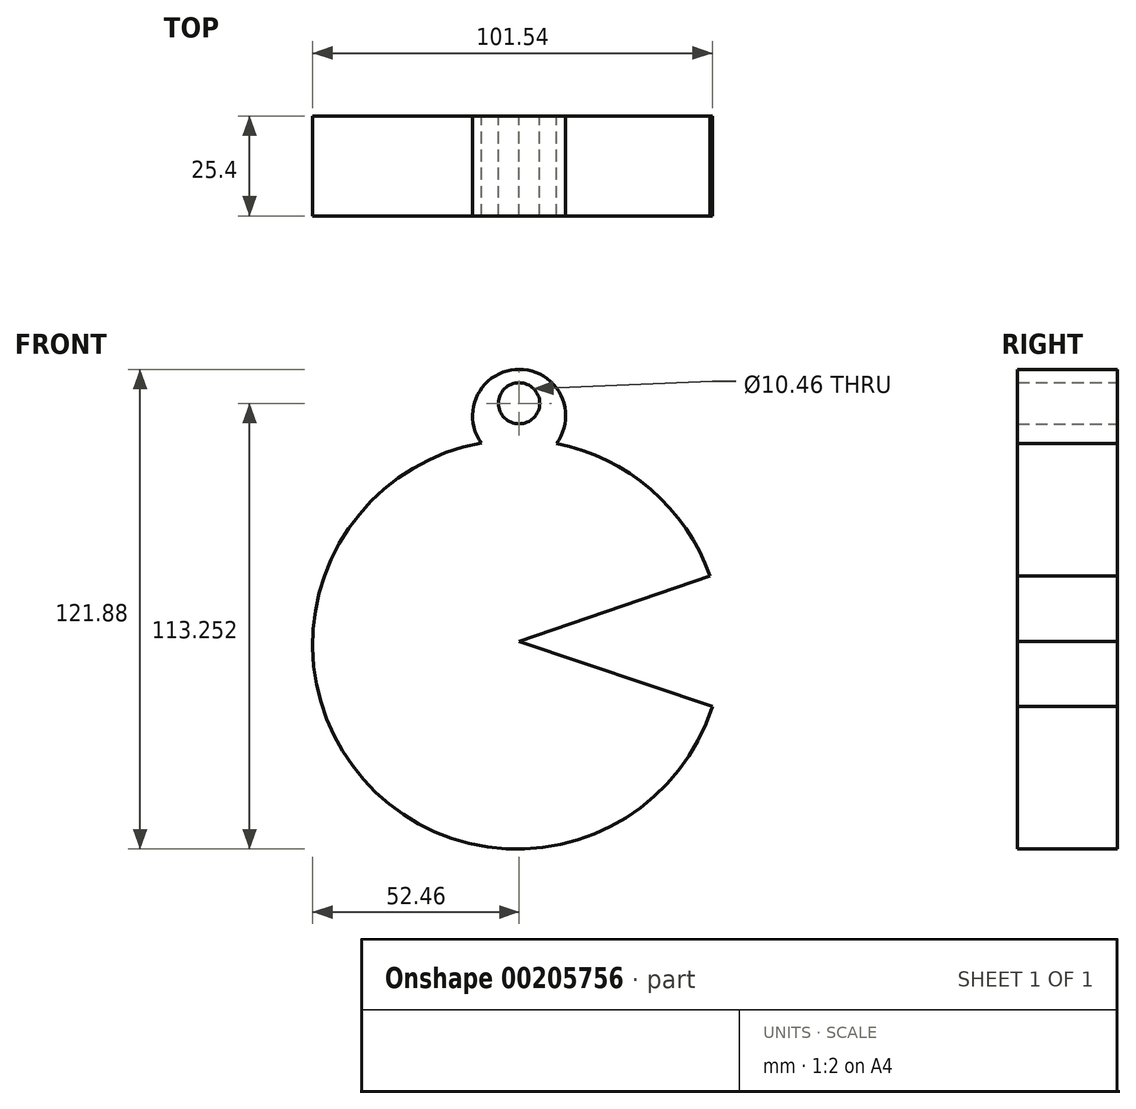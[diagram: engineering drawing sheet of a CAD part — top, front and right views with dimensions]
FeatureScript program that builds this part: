
annotation { "Feature Type Name" : "Feature", "Feature Type Description" : "" }
export const myFeature = defineFeature(function(context is Context, id is Id, definition is map)
    precondition{}
    {
        {
            var Q0;
            Q0=qCreatedBy(makeId("Front.planeOp"),FACE);
            var sketch = newSketch(context, id + "F0", { "sketchPlane" : qUnion([Q0])});
            skLineSegment(sketch, "E0", {"start": v(48.5, 16.7) * mm, "end": v(0, 0) * mm});
            skLineSegment(sketch, "E1", {"start": v(0, 0) * mm, "end": v(49.08, -16.4) * mm});
            skArc(sketch, "E2", {"start": v(48.5, 16.7) * mm, "mid": v(33.45, 38.67) * mm, "end": v(9.49, 50.3) * mm});
            skPoint(sketch, "E3.center.orphan", {"position": v(0, 60.55) * mm});
            skArc(sketch, "E4", {"start": v(9.49, 50.3) * mm, "mid": v(0.1, 69.18) * mm, "end": v(-9.6, 50.46) * mm});
            skArc(sketch, "E5.trimOffspring", {"start": v(-9.6, 50.46) * mm, "mid": v(-39.55, -35) * mm, "end": v(49.08, -16.4) * mm});
            skCircle(sketch, "E6", {"center": v(0, 60.55) * mm, "radius": 5.23 * mm});
            skSolve(sketch);
        }
        {
            var Q0;
            Q0=makeQuery(id+"F0.imprint","IMPRINT",FACE,{"disambiguationData":[TD([[makeQuery(id+"F0.imprint","IMPRINT",EDGE,{"derivedFrom":sQuery(id+"F0.wireOp",EDGE,"E0")}),-1.0]])]});
            extrude(context, id + "F1", {"entities" : qUnion([Q0]), "depth" : 25.4 * mm});
        }
        {
            var Q0;
            Q0=makeQuery(id+"F0.imprint","IMPRINT",FACE,{"disambiguationData":[TD([[makeQuery(id+"F0.imprint","IMPRINT",EDGE,{"derivedFrom":sQuery(id+"F0.wireOp",EDGE,"E0")}),-1.0]])]});
            var Q1;
            Q1=makeQuery(id+"F0.imprint","IMPRINT",FACE,{"disambiguationData":[TD([[makeQuery(id+"F0.imprint","IMPRINT",EDGE,{"derivedFrom":sQuery(id+"F0.wireOp",EDGE,"E3")}),1.0]])]});
            extrude(context, id + "F2", {"entities" : qUnion([Q0, Q1]), "operationType" : NewBodyOperationType.ADD, "depth" : 25.4 * mm});
        }
    });
